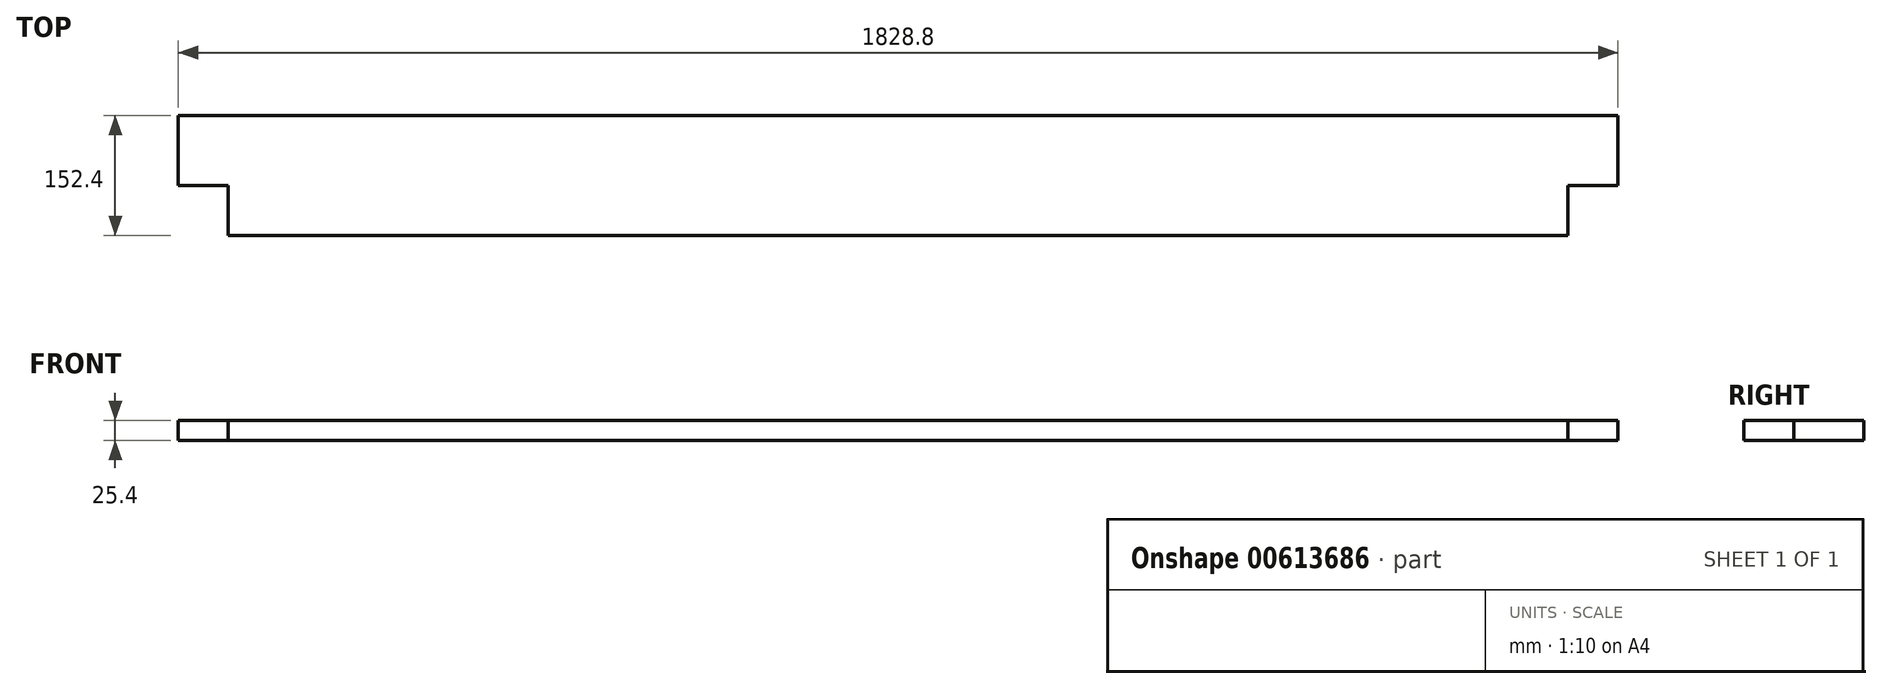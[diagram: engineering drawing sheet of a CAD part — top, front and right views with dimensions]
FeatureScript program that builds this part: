
annotation { "Feature Type Name" : "Feature", "Feature Type Description" : "" }
export const myFeature = defineFeature(function(context is Context, id is Id, definition is map)
    precondition{}
    {
        {
            var Q0;
            Q0=qCreatedBy(makeId("Top.planeOp"),FACE);
            var sketch = newSketch(context, id + "F0", { "sketchPlane" : qUnion([Q0])});
            skLineSegment(sketch, "E0.bottom", {"start": v(-912.58, -188.2) * mm, "end": v(916.22, -188.2) * mm});
            skLineSegment(sketch, "E0.top", {"start": v(-912.58, -340.6) * mm, "end": v(916.22, -340.6) * mm});
            skLineSegment(sketch, "E0.left", {"start": v(-912.58, -188.2) * mm, "end": v(-912.58, -340.6) * mm});
            skLineSegment(sketch, "E0.right", {"start": v(916.22, -188.2) * mm, "end": v(916.22, -340.6) * mm});
            skSolve(sketch);
        }
        {
            var Q0;
            Q0 = qSketchRegion(id + "F0", true);
            extrude(context, id + "F1", {"entities" : qUnion([Q0]), "depth" : 25.4 * mm, "offsetDistance" : 25.4 * mm});
        }
        {
            var Q0;
            Q0=makeQuery(id+"F1.opExtrude","CAP_FACE",FACE,{"disambiguationData":[OSD([sQuery(id+"F0.wireOp",EDGE,"E0.bottom"),sQuery(id+"F0.wireOp",EDGE,"E0.top"),sQuery(id+"F0.wireOp",EDGE,"E0.left"),sQuery(id+"F0.wireOp",EDGE,"E0.right")])],"isStart":false});
            var sketch = newSketch(context, id + "F2", { "sketchPlane" : qUnion([Q0])});
            skLineSegment(sketch, "E1.bottom", {"start": v(-912.58, -340.6) * mm, "end": v(-849.08, -340.6) * mm});
            skLineSegment(sketch, "E1.top", {"start": v(-912.58, -277.1) * mm, "end": v(-849.08, -277.1) * mm});
            skLineSegment(sketch, "E1.left", {"start": v(-912.58, -340.6) * mm, "end": v(-912.58, -277.1) * mm});
            skLineSegment(sketch, "E1.right", {"start": v(-849.08, -340.6) * mm, "end": v(-849.08, -277.1) * mm});
            skLineSegment(sketch, "E2.bottom", {"start": v(916.22, -340.6) * mm, "end": v(852.72, -340.6) * mm});
            skLineSegment(sketch, "E2.top", {"start": v(916.22, -277.1) * mm, "end": v(852.72, -277.1) * mm});
            skLineSegment(sketch, "E2.left", {"start": v(916.22, -340.6) * mm, "end": v(916.22, -277.1) * mm});
            skLineSegment(sketch, "E2.right", {"start": v(852.72, -340.6) * mm, "end": v(852.72, -277.1) * mm});
            skSolve(sketch);
        }
        {
            var Q0;
            Q0=makeQuery(id+"F2.imprint","IMPRINT",FACE,{"disambiguationData":[TD([[makeQuery(id+"F2.imprint","IMPRINT",EDGE,{"derivedFrom":sQuery(id+"F2.wireOp",EDGE,"E1.bottom")}),1.0]])]});
            var Q1;
            Q1=makeQuery(id+"F2.imprint","IMPRINT",FACE,{"disambiguationData":[TD([[makeQuery(id+"F2.imprint","IMPRINT",EDGE,{"derivedFrom":sQuery(id+"F2.wireOp",EDGE,"E2.bottom")}),1.0]])]});
            extrude(context, id + "F3", {"entities" : qUnion([Q0, Q1]), "operationType" : NewBodyOperationType.REMOVE, "oppositeDirection" : true, "depth" : 121.92 * mm, "offsetDistance" : 25.4 * mm});
        }
    });
